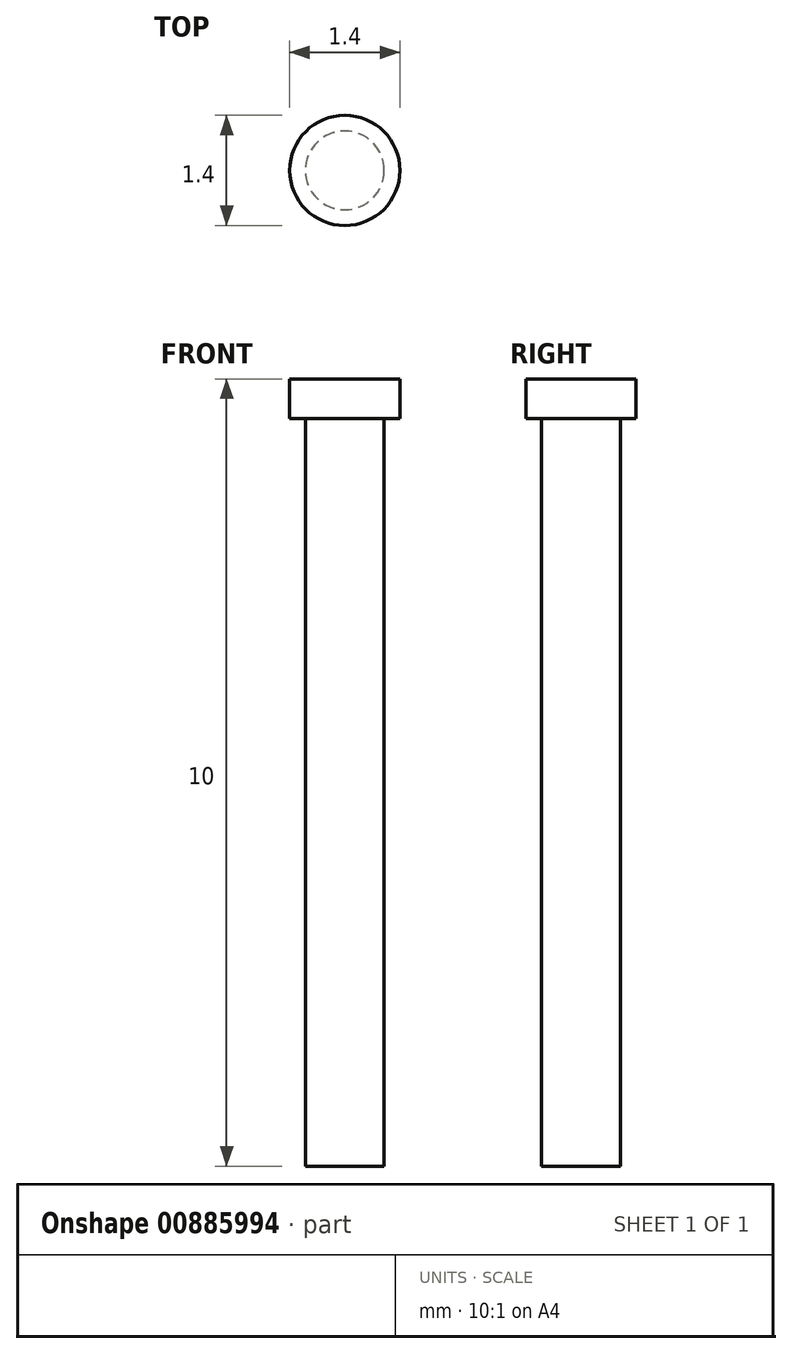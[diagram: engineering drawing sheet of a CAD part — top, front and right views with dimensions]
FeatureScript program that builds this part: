
annotation { "Feature Type Name" : "Feature", "Feature Type Description" : "" }
export const myFeature = defineFeature(function(context is Context, id is Id, definition is map)
    precondition{}
    {
        {
            var Q0;
            Q0=qCreatedBy(makeId("Front.planeOp"),FACE);
            var sketch = newSketch(context, id + "F0", { "sketchPlane" : qUnion([Q0])});
            skLineSegment(sketch, "E0", {"start": v(0, 0) * mm, "end": v(0.7, 0) * mm});
            skLineSegment(sketch, "E1", {"start": v(0.7, 0) * mm, "end": v(0.7, -0.5) * mm});
            skLineSegment(sketch, "E2", {"start": v(0.7, -0.5) * mm, "end": v(0.5, -0.5) * mm});
            skLineSegment(sketch, "E3", {"start": v(0.5, -0.5) * mm, "end": v(0.5, -10) * mm});
            skLineSegment(sketch, "E4", {"start": v(0.5, -10) * mm, "end": v(0, -10) * mm});
            skLineSegment(sketch, "E5", {"start": v(0, -10) * mm, "end": v(0, 0) * mm});
            skSolve(sketch);
        }
        {
            var Q0;
            Q0 = qSketchRegion(id + "F0", true);
            var Q1;
            Q1=sQuery(id+"F0.wireOp",EDGE,"E5");
            revolve(context, id + "F1", {"surfaceOperationType" : NewSurfaceOperationType.NEW, "entities" : qUnion([Q0]), "axis" : qUnion([Q1]), "revolveType" : RevolveType.FULL});
        }
    });
